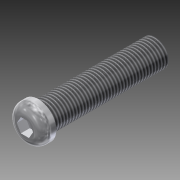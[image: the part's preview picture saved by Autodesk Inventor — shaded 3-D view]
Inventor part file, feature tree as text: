
AUTODESK INVENTOR PART (.ipt)
format: ipt  version: 2015 (Build 190159000, 159)  size: 115,200 bytes
history: native  units: mm
features: extrude x3, sketch x3, fillet x1, thread x1
ambient origin geometry x8: Origin, YZ Plane, XZ Plane, XY Plane, X Axis, Y Axis, Z Axis, Center Point
bodies: Solid1 (feature_tree)
feature tree (8):
  extrude  "Extrusion1"  Depth=1.5mm TaperAngle=0.0deg
  extrude  "Extrusion2"  Depth=13.0mm TaperAngle=0.0deg
  extrude  "Extrusion3"  Depth=1.0mm
  fillet  "Fillet1"  Radius=10.0mm
  thread  "Thread1"  [1 undecoded]
  sketch  "Sketch1"  dims[d0=4.0mm d1=1.5mm d2=0.0mm]
  sketch  "Sketch2"  dims[d3=3.0mm d4=13.0mm d5=0.0mm]
  sketch  "Sketch3"  dims[d6=1.0mm d7=0.0mm d8=1.0mm d9=10.0mm d10=0.0mm]
note: 1 required parameter value undecoded (feature->parameter linkage not recoverable at this tier; creation-order binding heuristic only, values carry confidence <= 0.55)
